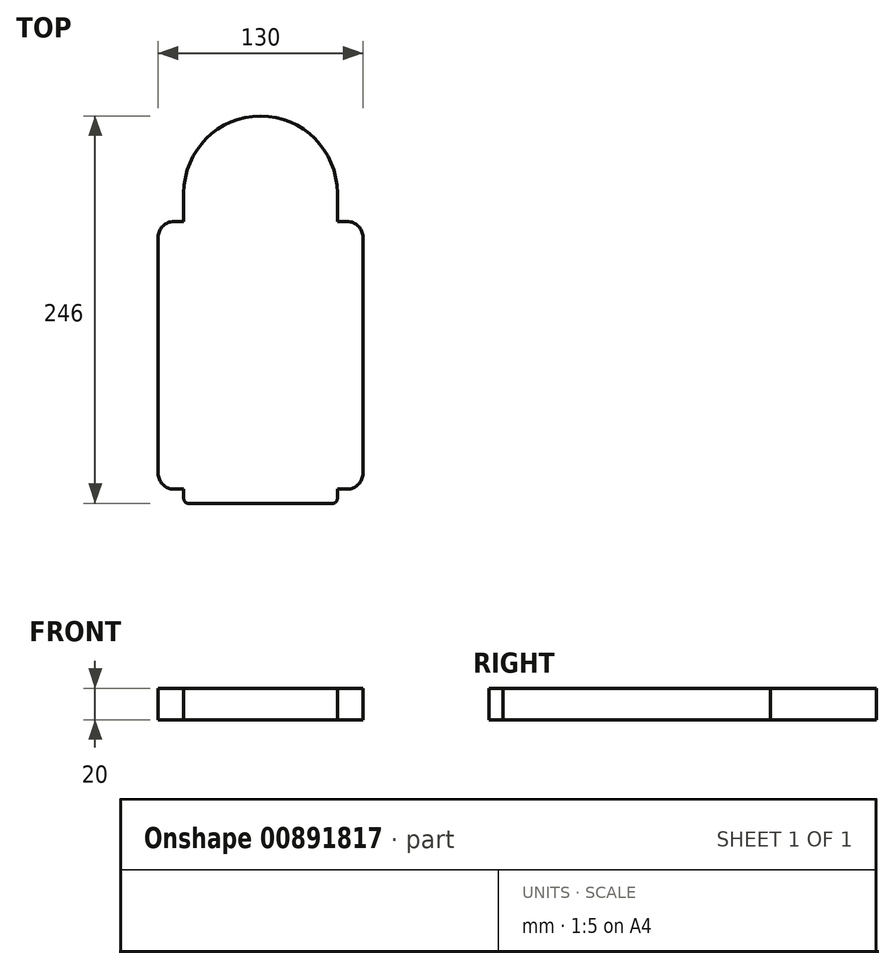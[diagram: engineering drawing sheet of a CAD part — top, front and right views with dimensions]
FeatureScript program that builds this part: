
annotation { "Feature Type Name" : "Feature", "Feature Type Description" : "" }
export const myFeature = defineFeature(function(context is Context, id is Id, definition is map)
    precondition{}
    {
        {
            var Q0;
            Q0=qCreatedBy(makeId("Top.planeOp"),FACE);
            var sketch = newSketch(context, id + "F0", { "sketchPlane" : qUnion([Q0])});
            skLineSegment(sketch, "E0", {"start": v(0, -120.5) * mm, "end": v(0, 120.5) * mm, "construction": true});
            skLineSegment(sketch, "E1", {"start": v(0, -120.5) * mm, "end": v(-41.75, -120.5) * mm});
            skLineSegment(sketch, "E2", {"start": v(-43.75, -118.5) * mm, "end": v(-43.75, -106.5) * mm});
            skLineSegment(sketch, "E3", {"start": v(-43.75, -106.5) * mm, "end": v(-55, -106.5) * mm});
            skLineSegment(sketch, "E4", {"start": v(-60, -101.5) * mm, "end": v(-60, 48.5) * mm});
            skLineSegment(sketch, "E5", {"start": v(-55, 53.5) * mm, "end": v(-43.75, 53.5) * mm});
            skLineSegment(sketch, "E6", {"start": v(-43.75, 53.5) * mm, "end": v(-43.75, 76.75) * mm});
            skArc(sketch, "E7", {"start": v(0, 120.5) * mm, "mid": v(-30.94, 107.69) * mm, "end": v(-43.75, 76.75) * mm});
            skLineSegment(sketch, "E8", {"start": v(-143.34, 120.5) * mm, "end": v(143.34, 120.5) * mm, "construction": true});
            skPoint(sketch, "E9.visualSharp", {"position": v(-43.75, -120.5) * mm});
            skArc(sketch, "E9.filletArc", {"start": v(-43.75, -118.5) * mm, "mid": v(-43.16, -119.91) * mm, "end": v(-41.75, -120.5) * mm});
            skPoint(sketch, "E10.visualSharp", {"position": v(-60, -106.5) * mm});
            skArc(sketch, "E10.filletArc", {"start": v(-60, -101.5) * mm, "mid": v(-58.54, -105.04) * mm, "end": v(-55, -106.5) * mm});
            skPoint(sketch, "E11.visualSharp", {"position": v(-60, 53.5) * mm});
            skArc(sketch, "E11.filletArc", {"start": v(-55, 53.5) * mm, "mid": v(-58.54, 52.04) * mm, "end": v(-60, 48.5) * mm});
            skArc(sketch, "E12.MirrorCS", {"start": v(0, 120.5) * mm, "mid": v(30.94, 107.69) * mm, "end": v(43.75, 76.75) * mm});
            skArc(sketch, "E13.MirrorCS", {"start": v(43.75, -118.5) * mm, "mid": v(43.16, -119.91) * mm, "end": v(41.75, -120.5) * mm});
            skArc(sketch, "E14.MirrorCS", {"start": v(55, 53.5) * mm, "mid": v(58.54, 52.04) * mm, "end": v(60, 48.5) * mm});
            skArc(sketch, "E15.MirrorCS", {"start": v(60, -101.5) * mm, "mid": v(58.54, -105.04) * mm, "end": v(55, -106.5) * mm});
            skLineSegment(sketch, "E16.MirrorCS", {"start": v(43.75, -118.5) * mm, "end": v(43.75, -106.5) * mm});
            skLineSegment(sketch, "E17.MirrorCS", {"start": v(60, -101.5) * mm, "end": v(60, 48.5) * mm});
            skPoint(sketch, "E18.MirrorP", {"position": v(60, -106.5) * mm});
            skPoint(sketch, "E19.MirrorP", {"position": v(43.75, -120.5) * mm});
            skPoint(sketch, "E20.MirrorP", {"position": v(60, 53.5) * mm});
            skLineSegment(sketch, "E21.MirrorCS", {"start": v(0, -120.5) * mm, "end": v(41.75, -120.5) * mm});
            skLineSegment(sketch, "E22.MirrorCS", {"start": v(43.75, -106.5) * mm, "end": v(55, -106.5) * mm});
            skLineSegment(sketch, "E23.MirrorCS", {"start": v(43.75, 53.5) * mm, "end": v(43.75, 76.75) * mm});
            skLineSegment(sketch, "E24.MirrorCS", {"start": v(55, 53.5) * mm, "end": v(43.75, 53.5) * mm});
            skLineSegment(sketch, "E25.0", {"start": v(0, -125.5) * mm, "end": v(41.75, -125.5) * mm, "construction": true});
            skArc(sketch, "E25.1", {"start": v(48.75, -118.5) * mm, "mid": v(46.7, -123.45) * mm, "end": v(41.75, -125.5) * mm, "construction": true});
            skLineSegment(sketch, "E25.2", {"start": v(48.75, -118.5) * mm, "end": v(48.75, -111.5) * mm, "construction": true});
            skLineSegment(sketch, "E25.3", {"start": v(48.75, -111.5) * mm, "end": v(55, -111.5) * mm});
            skArc(sketch, "E25.4", {"start": v(65, -101.5) * mm, "mid": v(62.07, -108.57) * mm, "end": v(55, -111.5) * mm});
            skLineSegment(sketch, "E25.5", {"start": v(0, -125.5) * mm, "end": v(-41.75, -125.5) * mm, "construction": true});
            skLineSegment(sketch, "E25.6", {"start": v(65, -101.5) * mm, "end": v(65, 48.5) * mm});
            skArc(sketch, "E25.7", {"start": v(55, 58.5) * mm, "mid": v(62.07, 55.57) * mm, "end": v(65, 48.5) * mm});
            skLineSegment(sketch, "E25.8", {"start": v(55, 58.5) * mm, "end": v(48.75, 58.5) * mm});
            skLineSegment(sketch, "E25.9", {"start": v(48.75, 58.5) * mm, "end": v(48.75, 76.75) * mm});
            skArc(sketch, "E25.10", {"start": v(-65, -101.5) * mm, "mid": v(-62.07, -108.57) * mm, "end": v(-55, -111.5) * mm});
            skLineSegment(sketch, "E25.11", {"start": v(-48.75, -111.5) * mm, "end": v(-55, -111.5) * mm});
            skLineSegment(sketch, "E25.12", {"start": v(-48.75, -118.5) * mm, "end": v(-48.75, -111.5) * mm, "construction": true});
            skArc(sketch, "E25.13", {"start": v(-48.75, -118.5) * mm, "mid": v(-46.7, -123.45) * mm, "end": v(-41.75, -125.5) * mm, "construction": true});
            skLineSegment(sketch, "E25.14", {"start": v(-65, -101.5) * mm, "end": v(-65, 48.5) * mm});
            skArc(sketch, "E25.15", {"start": v(-55, 58.5) * mm, "mid": v(-62.07, 55.57) * mm, "end": v(-65, 48.5) * mm});
            skLineSegment(sketch, "E25.16", {"start": v(-55, 58.5) * mm, "end": v(-48.75, 58.5) * mm});
            skLineSegment(sketch, "E25.17", {"start": v(-48.75, 58.5) * mm, "end": v(-48.75, 76.75) * mm});
            skArc(sketch, "E25.18", {"start": v(0, 125.5) * mm, "mid": v(-34.47, 111.22) * mm, "end": v(-48.75, 76.75) * mm});
            skArc(sketch, "E25.19", {"start": v(0, 125.5) * mm, "mid": v(34.47, 111.22) * mm, "end": v(48.75, 76.75) * mm});
            skLineSegment(sketch, "E26", {"start": v(-41.75, -120.5) * mm, "end": v(-45.75, -120.5) * mm});
            skLineSegment(sketch, "E27", {"start": v(-48.75, -117.5) * mm, "end": v(-48.75, -111.5) * mm});
            skPoint(sketch, "E28.visualSharp", {"position": v(-48.75, -120.5) * mm});
            skArc(sketch, "E28.filletArc", {"start": v(-48.75, -117.5) * mm, "mid": v(-47.87, -119.62) * mm, "end": v(-45.75, -120.5) * mm});
            skLineSegment(sketch, "E29.MirrorCS", {"start": v(41.75, -120.5) * mm, "end": v(45.75, -120.5) * mm});
            skArc(sketch, "E30.MirrorCS", {"start": v(48.75, -117.5) * mm, "mid": v(47.87, -119.62) * mm, "end": v(45.75, -120.5) * mm});
            skLineSegment(sketch, "E31.MirrorCS", {"start": v(48.75, -117.5) * mm, "end": v(48.75, -111.5) * mm});
            skSolve(sketch);
        }
        {
            var Q0;
            Q0=makeQuery(id+"F0.imprint","IMPRINT",FACE,{"disambiguationData":[TD([[makeQuery(id+"F0.imprint","IMPRINT",EDGE,{"derivedFrom":sQuery(id+"F0.wireOp",EDGE,"E1")}),1.0]])]});
            var Q1;
            Q1=makeQuery(id+"F0.imprint","IMPRINT",FACE,{"disambiguationData":[TD([[makeQuery(id+"F0.imprint","IMPRINT",EDGE,{"derivedFrom":sQuery(id+"F0.wireOp",EDGE,"E1")}),-1.0]])]});
            var Q2;
            Q2=makeQuery(id+"F0.imprint","IMPRINT",FACE,{"disambiguationData":[TD([[makeQuery(id+"F0.imprint","IMPRINT",EDGE,{"derivedFrom":sQuery(id+"F0.wireOp",EDGE,"E2")}),1.0]])]});
            extrude(context, id + "F1", {"entities" : qUnion([Q0, Q1, Q2]), "depth" : 20 * mm, "offsetDistance" : 25 * mm});
        }
    });
